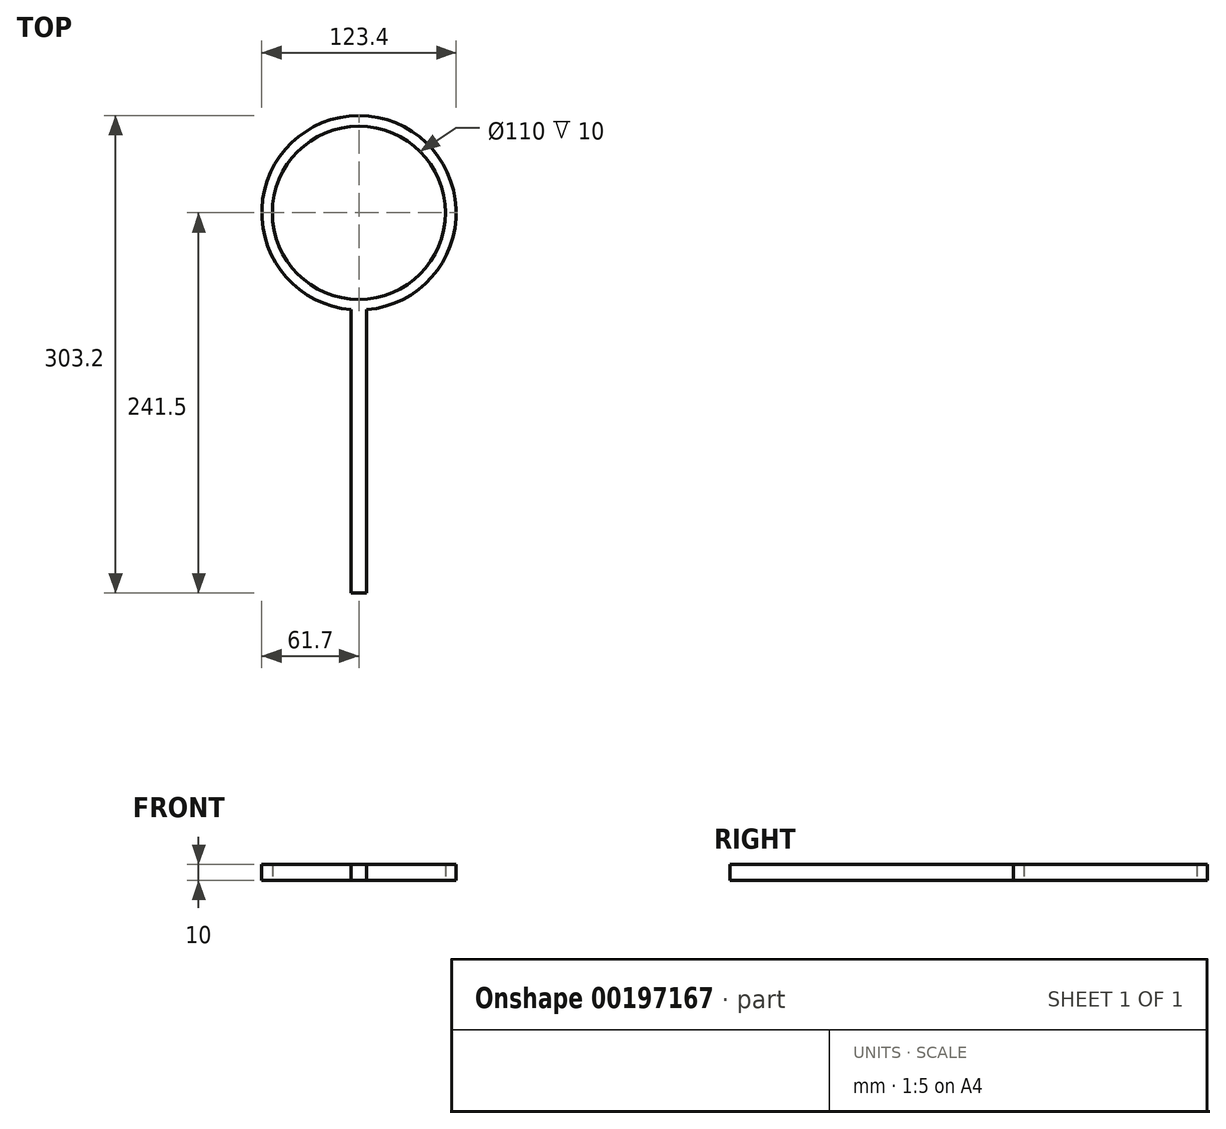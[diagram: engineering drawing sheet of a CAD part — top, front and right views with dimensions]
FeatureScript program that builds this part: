
annotation { "Feature Type Name" : "Feature", "Feature Type Description" : "" }
export const myFeature = defineFeature(function(context is Context, id is Id, definition is map)
    precondition{}
    {
        {
            var Q0;
            Q0=qCreatedBy(makeId("Top.planeOp"),FACE);
            var sketch = newSketch(context, id + "F0", { "sketchPlane" : qUnion([Q0])});
            skLineSegment(sketch, "E0", {"start": v(0, 0) * mm, "end": v(0, -180) * mm});
            skLineSegment(sketch, "E1", {"start": v(0, -180) * mm, "end": v(10, -180) * mm});
            skLineSegment(sketch, "E2", {"start": v(10, -180) * mm, "end": v(10, 0) * mm});
            skLineSegment(sketch, "E3", {"start": v(10, 0) * mm, "end": v(10, 61.5) * mm, "construction": true});
            skLineSegment(sketch, "E4", {"start": v(10, 61.5) * mm, "end": v(5, 61.5) * mm, "construction": true});
            skArc(sketch, "E5", {"start": v(10, 0) * mm, "mid": v(5, 123.2) * mm, "end": v(0, 0) * mm});
            skCircle(sketch, "E6", {"center": v(5, 61.5) * mm, "radius": 55 * mm});
            skSolve(sketch);
        }
        {
            var Q0;
            Q0=makeQuery(id+"F0.imprint","IMPRINT",FACE,{"disambiguationData":[TD([[makeQuery(id+"F0.imprint","IMPRINT",EDGE,{"derivedFrom":sQuery(id+"F0.wireOp",EDGE,"E0")}),1.0]])]});
            extrude(context, id + "F1", {"entities" : qUnion([Q0]), "depth" : 10 * mm});
        }
    });
